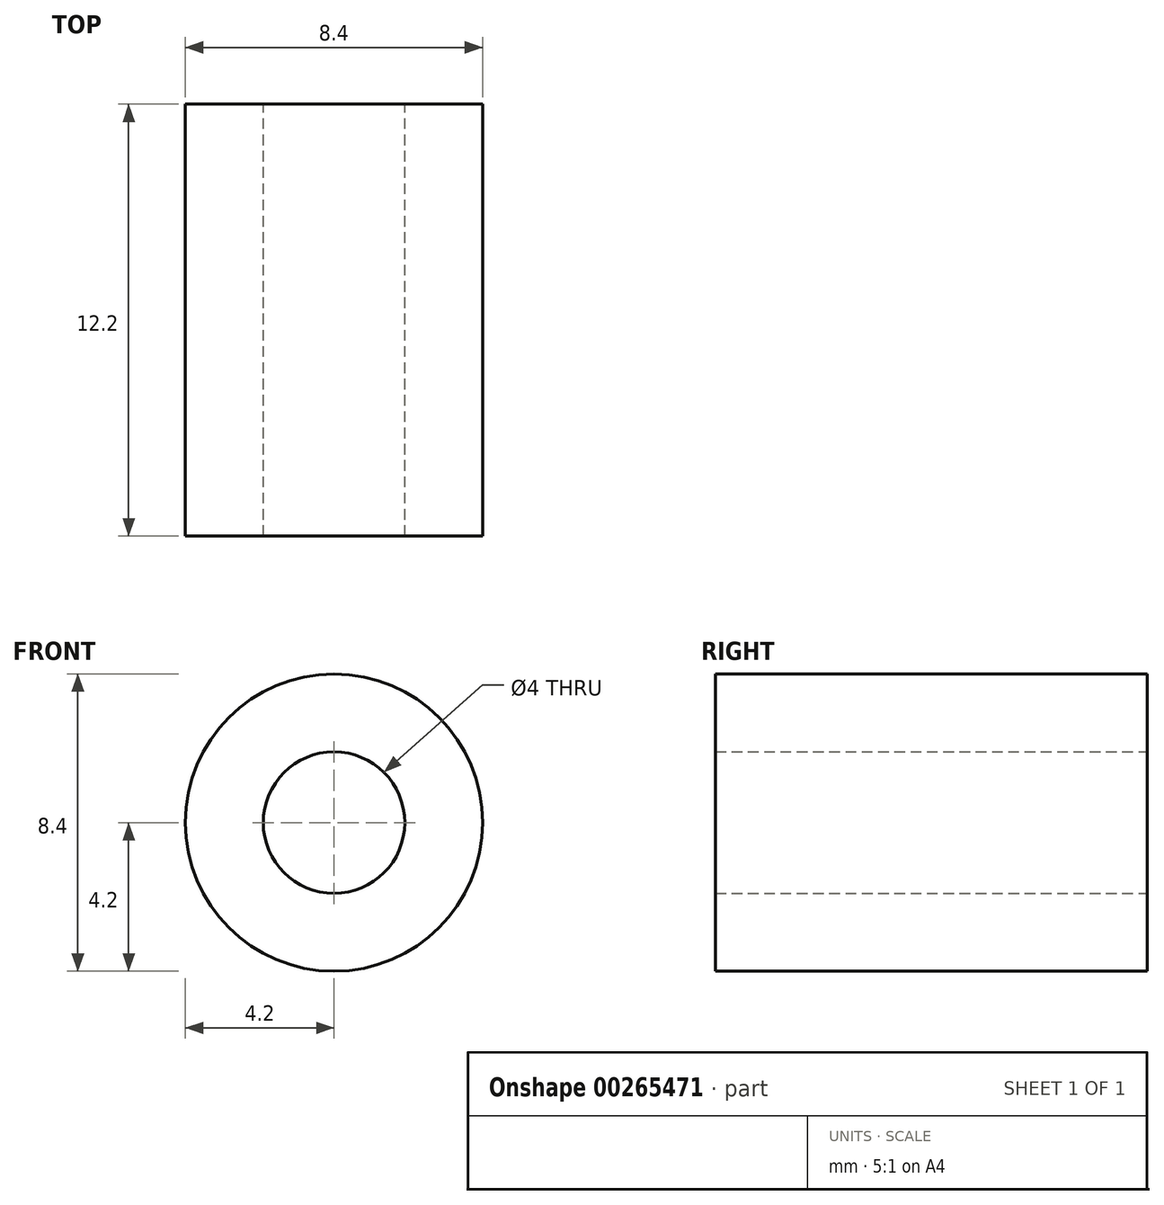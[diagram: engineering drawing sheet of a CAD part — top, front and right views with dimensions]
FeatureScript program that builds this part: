
annotation { "Feature Type Name" : "Feature", "Feature Type Description" : "" }
export const myFeature = defineFeature(function(context is Context, id is Id, definition is map)
    precondition{}
    {
        {
            var Q0;
            Q0=qCreatedBy(makeId("Front.planeOp"),FACE);
            var sketch = newSketch(context, id + "F0", { "sketchPlane" : qUnion([Q0])});
            skCircle(sketch, "E0", {"center": v(0, 0) * mm, "radius": 2 * mm});
            skCircle(sketch, "E1", {"center": v(0, 0) * mm, "radius": 4.2 * mm});
            skSolve(sketch);
        }
        {
            var Q0;
            Q0=makeQuery(id+"F0.imprint","IMPRINT",FACE,{"disambiguationData":[TD([[makeQuery(id+"F0.imprint","IMPRINT",EDGE,{"derivedFrom":sQuery(id+"F0.wireOp",EDGE,"E0")}),-1.0]])]});
            extrude(context, id + "F1", {"entities" : qUnion([Q0]), "depth" : 12.2 * mm});
        }
    });
